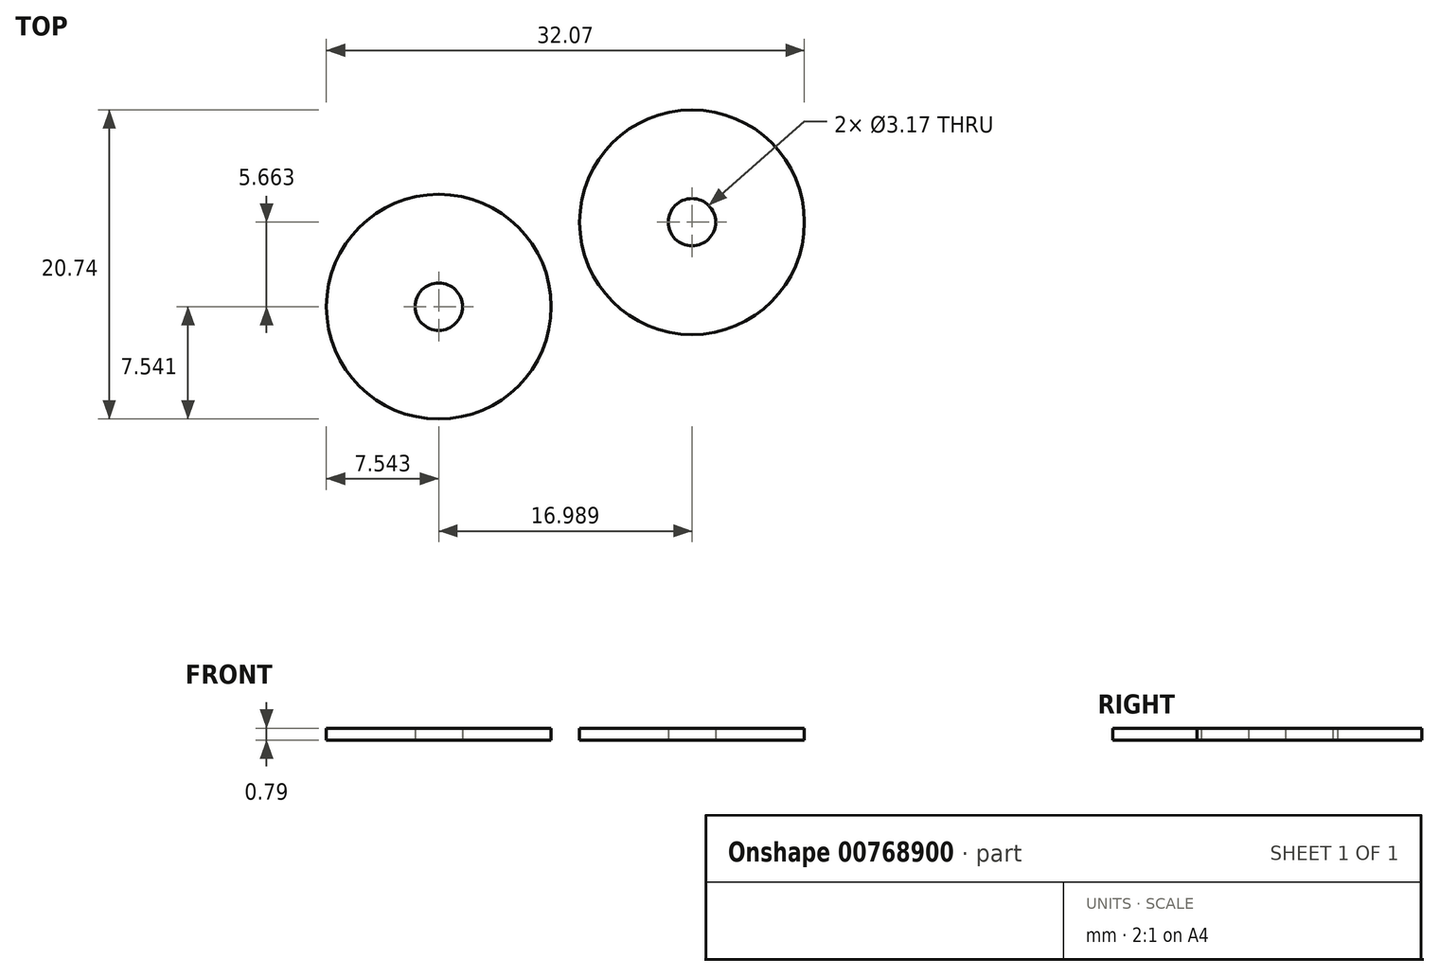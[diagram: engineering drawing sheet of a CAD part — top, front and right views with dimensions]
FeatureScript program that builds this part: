
annotation { "Feature Type Name" : "Feature", "Feature Type Description" : "" }
export const myFeature = defineFeature(function(context is Context, id is Id, definition is map)
    precondition{}
    {
        {
            var Q0;
            Q0=qCreatedBy(makeId("Top.planeOp"),FACE);
            var sketch = newSketch(context, id + "F0", { "sketchPlane" : qUnion([Q0])});
            skCircle(sketch, "E0", {"center": v(-22.64, 45.9) * mm, "radius": 7.54 * mm});
            skCircle(sketch, "E1", {"center": v(-22.64, 45.9) * mm, "radius": 1.59 * mm});
            skCircle(sketch, "E2", {"center": v(-5.65, 51.56) * mm, "radius": 7.54 * mm});
            skCircle(sketch, "E3", {"center": v(-5.65, 51.56) * mm, "radius": 1.59 * mm});
            skSolve(sketch);
        }
        {
            var Q0;
            Q0=makeQuery(id+"F0.imprint","IMPRINT",FACE,{"disambiguationData":[TD([[makeQuery(id+"F0.imprint","IMPRINT",EDGE,{"derivedFrom":sQuery(id+"F0.wireOp",EDGE,"E0")}),1.0]])]});
            var Q1;
            Q1=makeQuery(id+"F0.imprint","IMPRINT",FACE,{"disambiguationData":[TD([[makeQuery(id+"F0.imprint","IMPRINT",EDGE,{"derivedFrom":sQuery(id+"F0.wireOp",EDGE,"E2")}),1.0]])]});
            extrude(context, id + "F1", {"entities" : qUnion([Q0, Q1]), "depth" : 0.8 * mm, "offsetDistance" : 25.4 * mm});
        }
    });
